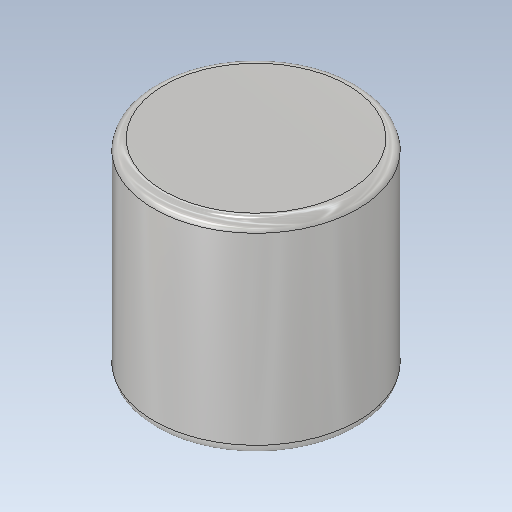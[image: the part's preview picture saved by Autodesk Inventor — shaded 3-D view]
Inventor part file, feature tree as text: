
AUTODESK INVENTOR PART (.ipt)
format: ipt  version: 2020.1 (Build 241239000, 239)  size: 133,632 bytes
history: native  units: mm
features: extrude x1, fillet x1, sketch x1
ambient origin geometry x8: Origin, YZ Plane, XZ Plane, XY Plane, X Axis, Y Axis, Z Axis, Center Point
bodies: Solid1 (feature_tree)
feature tree (3):
  extrude  "Extrusion1"  Depth=5.0mm TaperAngle=0.0deg
  fillet  "Fillet1"  Radius=0.25mm
  sketch  "Sketch1"  dims[d0=5.0mm d1=5.0mm d2=0.0mm d3=0.25mm]
